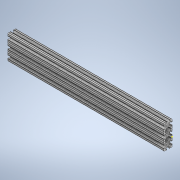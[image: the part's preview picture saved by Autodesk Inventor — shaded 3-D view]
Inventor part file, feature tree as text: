
AUTODESK INVENTOR PART (.ipt)
format: ipt  version: 2020 (Build 240168000, 168)  size: 375,296 bytes
history: native  units: in
note: dims shown in document units (in); Inventor stores cm internally (conversion verified against a paired STEP export)
features: sketch x2, extrude x1
ambient origin geometry x8: Origin, YZ Plane, XZ Plane, XY Plane, X Axis, Y Axis, Z Axis, Center Point
bodies: Solid1 (feature_tree)
feature tree (3):
  extrude  "Extrusion1"  [1 undecoded]
  sketch  "Sketch2"
  sketch  "Sketch1"  dims[d0=19.0in d1=0.0in]
note: 1 required parameter value undecoded (feature->parameter linkage not recoverable at this tier; creation-order binding heuristic only, values carry confidence <= 0.55)
